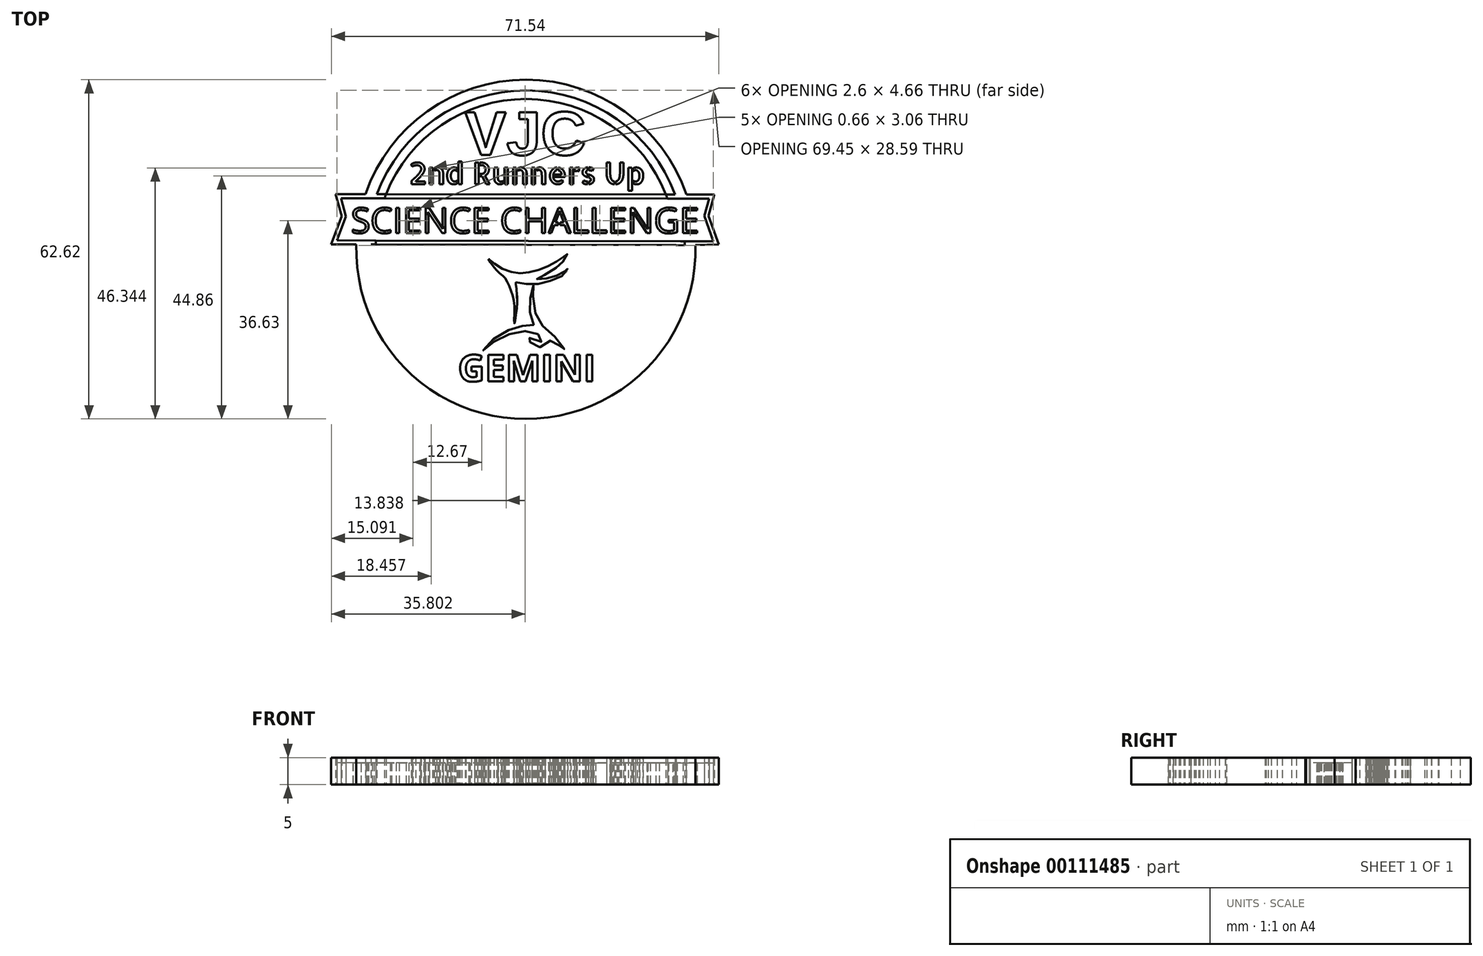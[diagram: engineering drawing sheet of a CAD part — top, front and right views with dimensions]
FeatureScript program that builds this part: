
annotation { "Feature Type Name" : "Feature", "Feature Type Description" : "" }
export const myFeature = defineFeature(function(context is Context, id is Id, definition is map)
    precondition{}
    {
        {
            var Q0;
            Q0=qCreatedBy(makeId("Top.planeOp"),FACE);
            var sketch = newSketch(context, id + "F0", { "sketchPlane" : qUnion([Q0])});
            skCircle(sketch, "E0", {"center": v(0.94, -3) * mm, "radius": 27.74 * mm});
            skPoint(sketch, "E0.first.point", {"position": v(1.58, 24.74) * mm});
            skPoint(sketch, "E0.second.point", {"position": v(0.52, -30.73) * mm});
            skPoint(sketch, "E0.third.point", {"position": v(-26.76, -1.33) * mm});
            skLineSegment(sketch, "E1", {"start": v(-24.87, 7.2) * mm, "end": v(-34.2, 7.2) * mm});
            skLineSegment(sketch, "E2", {"start": v(-34.2, 7.2) * mm, "end": v(-33.08, 3.11) * mm});
            skLineSegment(sketch, "E3", {"start": v(-33.08, 3.11) * mm, "end": v(-35, -2.1) * mm});
            skLineSegment(sketch, "E4", {"start": v(-35, -2.1) * mm, "end": v(-26.8, -2.1) * mm});
            skLineSegment(sketch, "E5", {"start": v(26.78, 7.1) * mm, "end": v(35.71, 7.1) * mm});
            skLineSegment(sketch, "E6", {"start": v(35.71, 7.1) * mm, "end": v(34.66, 3.21) * mm});
            skLineSegment(sketch, "E7", {"start": v(34.66, 3.21) * mm, "end": v(36.55, -2.1) * mm});
            skLineSegment(sketch, "E8", {"start": v(36.55, -2.1) * mm, "end": v(28.67, -2.25) * mm});
            skFitSpline(sketch, "E9", {"points": [v(-6, -4.72) * mm, v(-5.23, -5.35) * mm, v(-3.9, -6.35) * mm, v(-2.48, -6.98) * mm, v(-0.85, -7.35) * mm, v(0.35, -7.37) * mm, v(2.08, -7.15) * mm, v(3.86, -6.6) * mm, v(5.5, -5.84) * mm, v(6.83, -5.05) * mm, v(7.95, -4.34) * mm, v(8.2, -4.17) * mm, v(8.54, -3.89) * mm, v(8.14, -4.78) * mm, v(7.2, -5.82) * mm, v(5.2, -7.28) * mm, v(2.9, -8.45) * mm, v(3.98, -8.47) * mm, v(5.87, -8.12) * mm, v(7.76, -7.26) * mm, v(8.43, -6.75) * mm, v(8.6, -6.46) * mm, v(8.47, -7.15) * mm, v(6.46, -8.4) * mm, v(3.8, -9.28) * mm, v(1.11, -9.42) * mm, v(-0.95, -9.06) * mm], "startDerivative": vector(22.31, -18.25) * mm, "endDerivative": vector(-43, 9.84) * mm});
            skFitSpline(sketch, "E10", {"points": [v(-6, -4.72) * mm, v(-5.19, -6.01) * mm, v(-3.81, -7.48) * mm, v(-3.02, -8.2) * mm, v(-2.26, -9.47) * mm, v(-1.53, -11.45) * mm, v(-1.17, -13.95) * mm, v(-1.2, -16.67) * mm, v(-0.95, -15.45) * mm, v(-0.68, -11.98) * mm, v(-0.91, -9.36) * mm, v(-0.95, -9.06) * mm], "startDerivative": vector(8.3, -15) * mm, "endDerivative": vector(-0.86, 6) * mm});
            skFitSpline(sketch, "E11", {"points": [v(2.34, -9.66) * mm, v(2.02, -10.62) * mm, v(1.67, -12.76) * mm, v(1.67, -14.3) * mm, v(2.06, -16.19) * mm, v(2.36, -16.95) * mm, v(1.82, -16.92) * mm, v(-0.01, -17.17) * mm, v(-1.66, -17.64) * mm, v(-3.97, -18.79) * mm, v(-6.02, -20.44) * mm, v(-6.96, -21.68) * mm, v(-5.91, -20.77) * mm, v(-3.67, -19.33) * mm, v(-1.3, -18.4) * mm, v(0.83, -18.07) * mm, v(2.42, -18.3) * mm, v(3.7, -19.03) * mm, v(4.04, -19.68) * mm, v(3.45, -20.21) * mm, v(1.98, -19.81) * mm, v(1.3, -18.87) * mm, v(1.45, -19.8) * mm, v(2.36, -20.56) * mm, v(3.3, -21.02) * mm, v(4.84, -20.7) * mm, v(5.53, -19.8) * mm, v(6.38, -20.28) * mm, v(7.16, -20.84) * mm, v(8.14, -21.87) * mm, v(7.64, -20.68) * mm, v(6.28, -19.14) * mm, v(4.5, -17.53) * mm, v(3.33, -16.29) * mm, v(2.56, -14.18) * mm, v(2.24, -11.68) * mm, v(2.33, -10.24) * mm, v(2.34, -9.66) * mm]});
            skLineSegment(sketch, "E12", {"start": v(-24.87, 7.2) * mm, "end": v(28.1, 7.1) * mm});
            skLineSegment(sketch, "E13", {"start": v(-27.68, -2.1) * mm, "end": v(29.48, -2.24) * mm});
            skCircle(sketch, "E14.0", {"center": v(0.94, -3) * mm, "radius": 29.33 * mm});
            skCircle(sketch, "E15.0", {"center": v(0.94, -3) * mm, "radius": 31.31 * mm});
            skLineSegment(sketch, "E16.0", {"start": v(-24.87, 6.45) * mm, "end": v(28.1, 6.35) * mm});
            skLineSegment(sketch, "E17.0", {"start": v(-24.87, 6.45) * mm, "end": v(-33.21, 6.45) * mm});
            skLineSegment(sketch, "E18", {"start": v(28.1, 6.35) * mm, "end": v(34.73, 6.35) * mm});
            skLineSegment(sketch, "E19.0", {"start": v(-27.68, -1.35) * mm, "end": v(29.48, -1.49) * mm});
            skLineSegment(sketch, "E20", {"start": v(-27.68, -1.35) * mm, "end": v(-33.91, -1.33) * mm});
            skLineSegment(sketch, "E21", {"start": v(29.48, -1.49) * mm, "end": v(35.54, -1.5) * mm});
            skLineSegment(sketch, "E22.0", {"start": v(34.73, 6.35) * mm, "end": v(33.88, 3.18) * mm});
            skLineSegment(sketch, "E23.0", {"start": v(33.88, 3.18) * mm, "end": v(35.54, -1.5) * mm});
            skLineSegment(sketch, "E24.0", {"start": v(-32.3, 3.08) * mm, "end": v(-33.91, -1.33) * mm});
            skLineSegment(sketch, "E25.trimOffspring", {"start": v(-33.21, 6.45) * mm, "end": v(-32.3, 3.08) * mm});
            skText(sketch, "E26", { "text": "SCIENCE CHALLENGE", "fontName": "OpenSans-Regular.ttf"});
            skText(sketch, "E27", { "text": "GEMINI", "fontName": "OpenSans-Bold.ttf"});
            skText(sketch, "E28", { "text": "VJC", "fontName": "Arimo-Bold.ttf"});
            skLineSegment(sketch, "E29", {"start": v(6.9, 1.33) * mm, "end": v(6.9, 2.22) * mm});
            skLineSegment(sketch, "E30", {"start": v(6.9, 2.22) * mm, "end": v(7.18, 2.22) * mm});
            skLineSegment(sketch, "E31", {"start": v(7.18, 2.22) * mm, "end": v(7.26, 2.22) * mm});
            skLineSegment(sketch, "E32", {"start": v(7.26, 2.22) * mm, "end": v(7.26, 1.34) * mm});
            skLineSegment(sketch, "E33", {"start": v(7.26, 1.34) * mm, "end": v(6.9, 1.33) * mm});
            skText(sketch, "E34", { "text": "2nd Runners Up", "fontName": "AllertaStencil-Regular.ttf"});
            const initialGuessF0  = {"E26": [-0.03136, 0, 1, 0, 0.0047], "E27": [-0.0116, -0.02738, 1, 0, 0.00494], "E28": [-0.01032, 0.01442, 1, 0, 0.00826], "E34": [-0.02066, 0.00903, 1, 0, 0.004]};
            skSetInitialGuess(sketch, initialGuessF0);
            skSolve(sketch);
        }
        {
            var Q0;
            Q0=makeQuery(id+"F0.imprint","IMPRINT",FACE,{"disambiguationData":[TD([[makeQuery(id+"F0.imprint","IMPRINT",EDGE,{"derivedFrom":sQuery(id+"F0.wireOp",EDGE,"f2c7ee9f-897c-4c1d-89b3-a48ac7c6bfa7.sketch_text.stroke-0")}),1.0]])]});
            var Q1;
            {var subQ0=sQuery(id+"F0.wireOp",EDGE,"E15.0");var subQ1=sQuery(id+"F0.wireOp",EDGE,"E1");var subQ2=makeQuery(id+"F0.imprint","INTERSECT",VERTEX,{"derivedFrom":[subQ1,subQ0]});Q1=makeQuery(id+"F0.imprint","IMPRINT",FACE,{"disambiguationData":[TD([[makeQuery(id+"F0.imprint","IMPRINT",EDGE,{"disambiguationData":[TD([[subQ2,1.0]])],"derivedFrom":subQ1}),-1.0]])]});}
            var Q2;
            Q2=makeQuery(id+"F0.imprint","IMPRINT",FACE,{"disambiguationData":[TD([[makeQuery(id+"F0.imprint","IMPRINT",EDGE,{"derivedFrom":sQuery(id+"F0.wireOp",EDGE,"26462852-2f77-49b2-9a3d-6dfd93b606f1.sketch_text.stroke-0")}),1.0]])]});
            var Q3;
            {var subQ0=sQuery(id+"F0.wireOp",EDGE,"E15.0");var subQ1=sQuery(id+"F0.wireOp",EDGE,"E4");var subQ2=makeQuery(id+"F0.imprint","INTERSECT",VERTEX,{"derivedFrom":[subQ1,subQ0]});Q3=makeQuery(id+"F0.imprint","IMPRINT",FACE,{"disambiguationData":[TD([[makeQuery(id+"F0.imprint","IMPRINT",EDGE,{"disambiguationData":[TD([[subQ2,-1.0]])],"derivedFrom":subQ1}),-1.0]])]});}
            var Q4;
            {var subQ7=sQuery(id+"F0.wireOp",EDGE,"E2");Q4=makeQuery(id+"F0.imprint","IMPRINT",FACE,{"disambiguationData":[TD([[makeQuery(id+"F0.imprint","IMPRINT",EDGE,{"derivedFrom":subQ7}),1.0]])]});}
            var Q5;
            {var subQ3=sQuery(id+"F0.wireOp",EDGE,"E17.0");var subQ10=makeQuery(id+"F0.imprint","IMPRINT",VERTEX,{"derivedFrom":subQ3});Q5=makeQuery(id+"F0.imprint","IMPRINT",FACE,{"disambiguationData":[TD([[makeQuery(id+"F0.imprint","IMPRINT",EDGE,{"disambiguationData":[TD([[subQ10,1.0]])],"derivedFrom":subQ3}),-1.0]])]});}
            var Q6;
            {var subQ0=sQuery(id+"F0.wireOp",EDGE,"E1");var subQ5=sQuery(id+"F0.wireOp",EDGE,"E14.0");var subQ6=makeQuery(id+"F0.imprint","INTERSECT",VERTEX,{"derivedFrom":[subQ0,subQ5]});Q6=makeQuery(id+"F0.imprint","IMPRINT",FACE,{"disambiguationData":[TD([[makeQuery(id+"F0.imprint","IMPRINT",EDGE,{"disambiguationData":[TD([[subQ6,-1.0]])],"derivedFrom":subQ5}),1.0]])]});}
            var Q7;
            {var subQ1=sQuery(id+"F0.wireOp",EDGE,"E5");var subQ6=sQuery(id+"F0.wireOp",EDGE,"E0");var subQ7=makeQuery(id+"F0.imprint","INTERSECT",VERTEX,{"derivedFrom":[subQ6,subQ1]});Q7=makeQuery(id+"F0.imprint","IMPRINT",FACE,{"disambiguationData":[TD([[makeQuery(id+"F0.imprint","IMPRINT",EDGE,{"disambiguationData":[TD([[subQ7,1.0]])],"derivedFrom":subQ6}),-1.0]])]});}
            var Q8;
            {var subQ0=sQuery(id+"F0.wireOp",EDGE,"E15.0");var subQ1=sQuery(id+"F0.wireOp",EDGE,"E5");var subQ2=makeQuery(id+"F0.imprint","INTERSECT",VERTEX,{"derivedFrom":[subQ1,subQ0]});Q8=makeQuery(id+"F0.imprint","IMPRINT",FACE,{"disambiguationData":[TD([[makeQuery(id+"F0.imprint","IMPRINT",EDGE,{"disambiguationData":[TD([[subQ2,1.0]])],"derivedFrom":subQ1}),-1.0]])]});}
            var Q9;
            {var subQ11=sQuery(id+"F0.wireOp",EDGE,"E6");Q9=makeQuery(id+"F0.imprint","IMPRINT",FACE,{"disambiguationData":[TD([[makeQuery(id+"F0.imprint","IMPRINT",EDGE,{"derivedFrom":subQ11}),-1.0]])]});}
            var Q10;
            {var subQ0=sQuery(id+"F0.wireOp",EDGE,"E13");var subQ1=sQuery(id+"F0.wireOp",EDGE,"E0");var subQ2=makeQuery(id+"F0.imprint","INTERSECT",VERTEX,{"disambiguationData":[OD(0.0)],"derivedFrom":[subQ1,subQ0]});Q10=makeQuery(id+"F0.imprint","IMPRINT",FACE,{"disambiguationData":[TD([[makeQuery(id+"F0.imprint","IMPRINT",EDGE,{"disambiguationData":[TD([[subQ2,-1.0]])],"derivedFrom":subQ1}),1.0]])]});}
            var Q11;
            {var subQ0=sQuery(id+"F0.wireOp",EDGE,"E13");var subQ3=sQuery(id+"F0.wireOp",EDGE,"E0");var subQ4=makeQuery(id+"F0.imprint","INTERSECT",VERTEX,{"disambiguationData":[OD(0.0)],"derivedFrom":[subQ3,subQ0]});Q11=makeQuery(id+"F0.imprint","IMPRINT",FACE,{"disambiguationData":[TD([[makeQuery(id+"F0.imprint","IMPRINT",EDGE,{"disambiguationData":[TD([[subQ4,-1.0]])],"derivedFrom":subQ3}),-1.0]])]});}
            var Q12;
            {var subQ0=sQuery(id+"F0.wireOp",EDGE,"E15.0");var subQ1=sQuery(id+"F0.wireOp",EDGE,"E8");var subQ2=makeQuery(id+"F0.imprint","INTERSECT",VERTEX,{"derivedFrom":[subQ1,subQ0]});Q12=makeQuery(id+"F0.imprint","IMPRINT",FACE,{"disambiguationData":[TD([[makeQuery(id+"F0.imprint","IMPRINT",EDGE,{"disambiguationData":[TD([[subQ2,-1.0]])],"derivedFrom":subQ1}),-1.0]])]});}
            var Q13;
            {var subQ0=sQuery(id+"F0.wireOp",EDGE,"E15.0");var subQ1=sQuery(id+"F0.wireOp",EDGE,"E1");var subQ2=makeQuery(id+"F0.imprint","INTERSECT",VERTEX,{"derivedFrom":[subQ1,subQ0]});Q13=makeQuery(id+"F0.imprint","IMPRINT",FACE,{"disambiguationData":[TD([[makeQuery(id+"F0.imprint","IMPRINT",EDGE,{"disambiguationData":[TD([[subQ2,1.0]])],"derivedFrom":subQ1}),1.0]])]});}
            var Q14;
            {var subQ0=sQuery(id+"F0.wireOp",EDGE,"E15.0");var subQ1=sQuery(id+"F0.wireOp",EDGE,"E4");var subQ2=makeQuery(id+"F0.imprint","INTERSECT",VERTEX,{"derivedFrom":[subQ1,subQ0]});Q14=makeQuery(id+"F0.imprint","IMPRINT",FACE,{"disambiguationData":[TD([[makeQuery(id+"F0.imprint","IMPRINT",EDGE,{"disambiguationData":[TD([[subQ2,-1.0]])],"derivedFrom":subQ1}),1.0]])]});}
            var Q15;
            {var subQ0=sQuery(id+"F0.wireOp",EDGE,"E4");var subQ1=sQuery(id+"F0.wireOp",EDGE,"E0");var subQ2=makeQuery(id+"F0.imprint","INTERSECT",VERTEX,{"derivedFrom":[subQ1,subQ0]});Q15=makeQuery(id+"F0.imprint","IMPRINT",FACE,{"disambiguationData":[TD([[makeQuery(id+"F0.imprint","IMPRINT",EDGE,{"disambiguationData":[TD([[subQ2,1.0]])],"derivedFrom":subQ1}),-1.0]])]});}
            var Q16;
            Q16=makeQuery(id+"F0.imprint","IMPRINT",FACE,{"disambiguationData":[TD([[makeQuery(id+"F0.imprint","IMPRINT",EDGE,{"derivedFrom":sQuery(id+"F0.wireOp",EDGE,"E9")}),1.0]])]});
            var Q17;
            Q17=makeQuery(id+"F0.imprint","IMPRINT",FACE,{"disambiguationData":[TD([[makeQuery(id+"F0.imprint","IMPRINT",EDGE,{"derivedFrom":sQuery(id+"F0.wireOp",EDGE,"E28.sketch_text.stroke-0")}),1.0]])]});
            extrude(context, id + "F1", {"entities" : qUnion([Q0, Q1, Q2, Q3, Q4, Q5, Q6, Q7, Q8, Q9, Q10, Q11, Q12, Q13, Q14, Q15, Q16, Q17]), "depth" : 5 * mm});
        }
        {
            var Q0;
            {var subQ0=sQuery(id+"F0.wireOp",EDGE,"E24.0");Q0=makeQuery(id+"F0.imprint","IMPRINT",FACE,{"disambiguationData":[TD([[makeQuery(id+"F0.imprint","IMPRINT",EDGE,{"derivedFrom":subQ0}),1.0]])]});}
            var Q1;
            {var subQ11=sQuery(id+"F0.wireOp",EDGE,"E26.sketch_text.stroke-16");Q1=makeQuery(id+"F0.imprint","IMPRINT",FACE,{"disambiguationData":[TD([[makeQuery(id+"F0.imprint","IMPRINT",EDGE,{"derivedFrom":subQ11}),1.0]])]});}
            var Q2;
            {var subQ0=sQuery(id+"F0.wireOp",EDGE,"E26.sketch_text.stroke-33");Q2=makeQuery(id+"F0.imprint","IMPRINT",FACE,{"disambiguationData":[TD([[makeQuery(id+"F0.imprint","IMPRINT",EDGE,{"derivedFrom":subQ0}),1.0]])]});}
            var Q3;
            {var subQ10=sQuery(id+"F0.wireOp",EDGE,"E26.sketch_text.stroke-28");Q3=makeQuery(id+"F0.imprint","IMPRINT",FACE,{"disambiguationData":[TD([[makeQuery(id+"F0.imprint","IMPRINT",EDGE,{"derivedFrom":subQ10}),1.0]])]});}
            var Q4;
            {var subQ25=sQuery(id+"F0.wireOp",EDGE,"E26.sketch_text.stroke-178");Q4=makeQuery(id+"F0.imprint","IMPRINT",FACE,{"disambiguationData":[TD([[makeQuery(id+"F0.imprint","IMPRINT",EDGE,{"derivedFrom":subQ25}),1.0]])]});}
            var Q5;
            {var subQ1=sQuery(id+"F0.wireOp",EDGE,"E26.sketch_text.stroke-198");var subQ3=sQuery(id+"F0.wireOp",EDGE,"E14.0");var subQ4=makeQuery(id+"F0.imprint","INTERSECT",VERTEX,{"derivedFrom":[subQ3,subQ1]});Q5=makeQuery(id+"F0.imprint","IMPRINT",FACE,{"disambiguationData":[TD([[makeQuery(id+"F0.imprint","IMPRINT",EDGE,{"disambiguationData":[TD([[subQ4,-1.0]])],"derivedFrom":subQ3}),-1.0]])]});}
            var Q6;
            {var subQ8=sQuery(id+"F0.wireOp",EDGE,"E22.0");Q6=makeQuery(id+"F0.imprint","IMPRINT",FACE,{"disambiguationData":[TD([[makeQuery(id+"F0.imprint","IMPRINT",EDGE,{"derivedFrom":subQ8}),-1.0]])]});}
            var Q7;
            {var subQ0=sQuery(id+"F0.wireOp",EDGE,"E26.sketch_text.stroke-6");Q7=makeQuery(id+"F0.imprint","IMPRINT",FACE,{"disambiguationData":[TD([[makeQuery(id+"F0.imprint","IMPRINT",EDGE,{"derivedFrom":subQ0}),1.0]])]});}
            var Q8;
            {var subQ6=sQuery(id+"F0.wireOp",EDGE,"E26.sketch_text.stroke-1");Q8=makeQuery(id+"F0.imprint","IMPRINT",FACE,{"disambiguationData":[TD([[makeQuery(id+"F0.imprint","IMPRINT",EDGE,{"derivedFrom":subQ6}),1.0]])]});}
            var Q9;
            {var subQ6=sQuery(id+"F0.wireOp",EDGE,"E26.sketch_text.stroke-189");Q9=makeQuery(id+"F0.imprint","IMPRINT",FACE,{"disambiguationData":[TD([[makeQuery(id+"F0.imprint","IMPRINT",EDGE,{"derivedFrom":subQ6}),1.0]])]});}
            var Q10;
            {var subQ5=sQuery(id+"F0.wireOp",EDGE,"E26.sketch_text.stroke-202");Q10=makeQuery(id+"F0.imprint","IMPRINT",FACE,{"disambiguationData":[TD([[makeQuery(id+"F0.imprint","IMPRINT",EDGE,{"derivedFrom":subQ5}),1.0]])]});}
            var Q11;
            {var subQ5=sQuery(id+"F0.wireOp",EDGE,"E26.sketch_text.stroke-206");Q11=makeQuery(id+"F0.imprint","IMPRINT",FACE,{"disambiguationData":[TD([[makeQuery(id+"F0.imprint","IMPRINT",EDGE,{"derivedFrom":subQ5}),1.0]])]});}
            var Q12;
            {var subQ0=sQuery(id+"F0.wireOp",EDGE,"E21");var subQ1=sQuery(id+"F0.wireOp",EDGE,"E14.0");var subQ2=makeQuery(id+"F0.imprint","INTERSECT",VERTEX,{"derivedFrom":[subQ1,subQ0]});Q12=makeQuery(id+"F0.imprint","IMPRINT",FACE,{"disambiguationData":[TD([[makeQuery(id+"F0.imprint","IMPRINT",EDGE,{"disambiguationData":[TD([[subQ2,-1.0]])],"derivedFrom":subQ1}),-1.0]])]});}
            var Q13;
            Q13=makeQuery(id+"F0.imprint","IMPRINT",FACE,{"disambiguationData":[TD([[makeQuery(id+"F0.imprint","IMPRINT",EDGE,{"derivedFrom":sQuery(id+"F0.wireOp",EDGE,"E26.sketch_text.stroke-133")}),1.0]])]});
            var Q14;
            {var subQ5=sQuery(id+"F0.wireOp",EDGE,"E26.sketch_text.stroke-26");Q14=makeQuery(id+"F0.imprint","IMPRINT",FACE,{"disambiguationData":[TD([[makeQuery(id+"F0.imprint","IMPRINT",EDGE,{"derivedFrom":subQ5}),1.0]])]});}
            var Q15;
            {var subQ1=sQuery(id+"F0.wireOp",EDGE,"E26.sketch_text.stroke-19");Q15=makeQuery(id+"F0.imprint","IMPRINT",FACE,{"disambiguationData":[TD([[makeQuery(id+"F0.imprint","IMPRINT",EDGE,{"derivedFrom":subQ1}),1.0]])]});}
            var Q16;
            {var subQ5=sQuery(id+"F0.wireOp",EDGE,"E33");Q16=makeQuery(id+"F0.imprint","IMPRINT",FACE,{"disambiguationData":[TD([[makeQuery(id+"F0.imprint","IMPRINT",EDGE,{"derivedFrom":subQ5}),-1.0]])]});}
            var Q17;
            {var subQ0=sQuery(id+"F0.wireOp",EDGE,"E32");var subQ1=sQuery(id+"F0.wireOp",EDGE,"E26.sketch_text.stroke-126");var subQ2=makeQuery(id+"F0.imprint","INTERSECT",VERTEX,{"derivedFrom":[subQ1,subQ0]});Q17=makeQuery(id+"F0.imprint","IMPRINT",FACE,{"disambiguationData":[TD([[makeQuery(id+"F0.imprint","IMPRINT",EDGE,{"disambiguationData":[TD([[subQ2,-1.0]])],"derivedFrom":subQ1}),-1.0]])]});}
            var Q18;
            {var subQ1=sQuery(id+"F0.wireOp",EDGE,"E30");Q18=makeQuery(id+"F0.imprint","IMPRINT",FACE,{"disambiguationData":[TD([[makeQuery(id+"F0.imprint","IMPRINT",EDGE,{"derivedFrom":subQ1}),-1.0]])]});}
            extrude(context, id + "F2", {"entities" : qUnion([Q0, Q1, Q2, Q3, Q4, Q5, Q6, Q7, Q8, Q9, Q10, Q11, Q12, Q13, Q14, Q15, Q16, Q17, Q18]), "depth" : 4 * mm});
        }
    });
